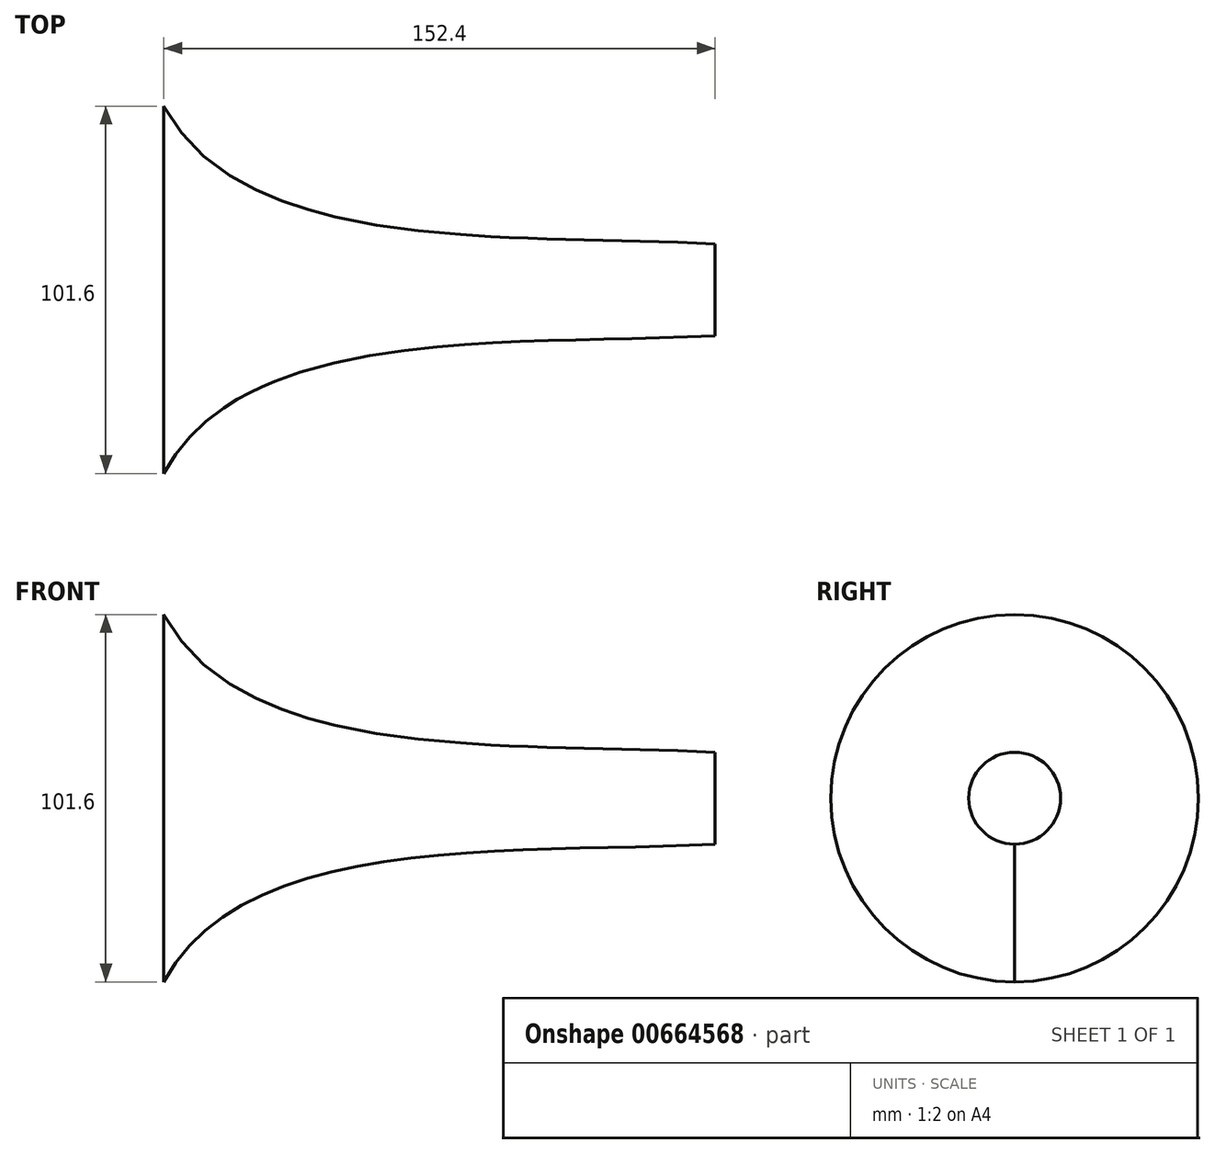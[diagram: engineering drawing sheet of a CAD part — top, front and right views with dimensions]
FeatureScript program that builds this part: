
annotation { "Feature Type Name" : "Feature", "Feature Type Description" : "" }
export const myFeature = defineFeature(function(context is Context, id is Id, definition is map)
    precondition{}
    {
        {
            var Q0;
            Q0=qCreatedBy(makeId("Front.planeOp"),FACE);
            var sketch = newSketch(context, id + "F0", { "sketchPlane" : qUnion([Q0])});
            skLineSegment(sketch, "E0.bottom", {"start": v(125.06, 35.04) * mm, "end": v(-27.34, 35.04) * mm});
            skLineSegment(sketch, "E0.top", {"start": v(125.06, 22.34) * mm, "end": v(-27.34, 22.34) * mm});
            skLineSegment(sketch, "E0.left", {"start": v(125.06, 35.04) * mm, "end": v(125.06, 22.34) * mm});
            skLineSegment(sketch, "E0.right", {"start": v(-27.34, 35.04) * mm, "end": v(-27.34, 22.34) * mm});
            skLineSegment(sketch, "E1", {"start": v(-27.34, 35.04) * mm, "end": v(-27.34, 73.14) * mm});
            skFitSpline(sketch, "E2", {"points": [v(-27.34, 73.14) * mm, v(125.06, 35.04) * mm], "startDerivative": vector(67.2, -126.54) * mm, "endDerivative": vector(160.68, -8.93) * mm});
            skSolve(sketch);
        }
        {
            var Q0;
            Q0=makeQuery(id+"F0.imprint","IMPRINT",FACE,{"disambiguationData":[TD([[makeQuery(id+"F0.imprint","IMPRINT",EDGE,{"derivedFrom":sQuery(id+"F0.wireOp",EDGE,"E0.bottom")}),1.0]])]});
            var Q1;
            Q1=makeQuery(id+"F0.imprint","IMPRINT",FACE,{"disambiguationData":[TD([[makeQuery(id+"F0.imprint","IMPRINT",EDGE,{"derivedFrom":sQuery(id+"F0.wireOp",EDGE,"E0.bottom")}),-1.0]])]});
            var Q2;
            Q2=sQuery(id+"F0.wireOp",EDGE,"E0.top");
            revolve(context, id + "F1", {"entities" : qUnion([Q0, Q1]), "axis" : qUnion([Q2]), "revolveType" : RevolveType.FULL});
        }
    });
